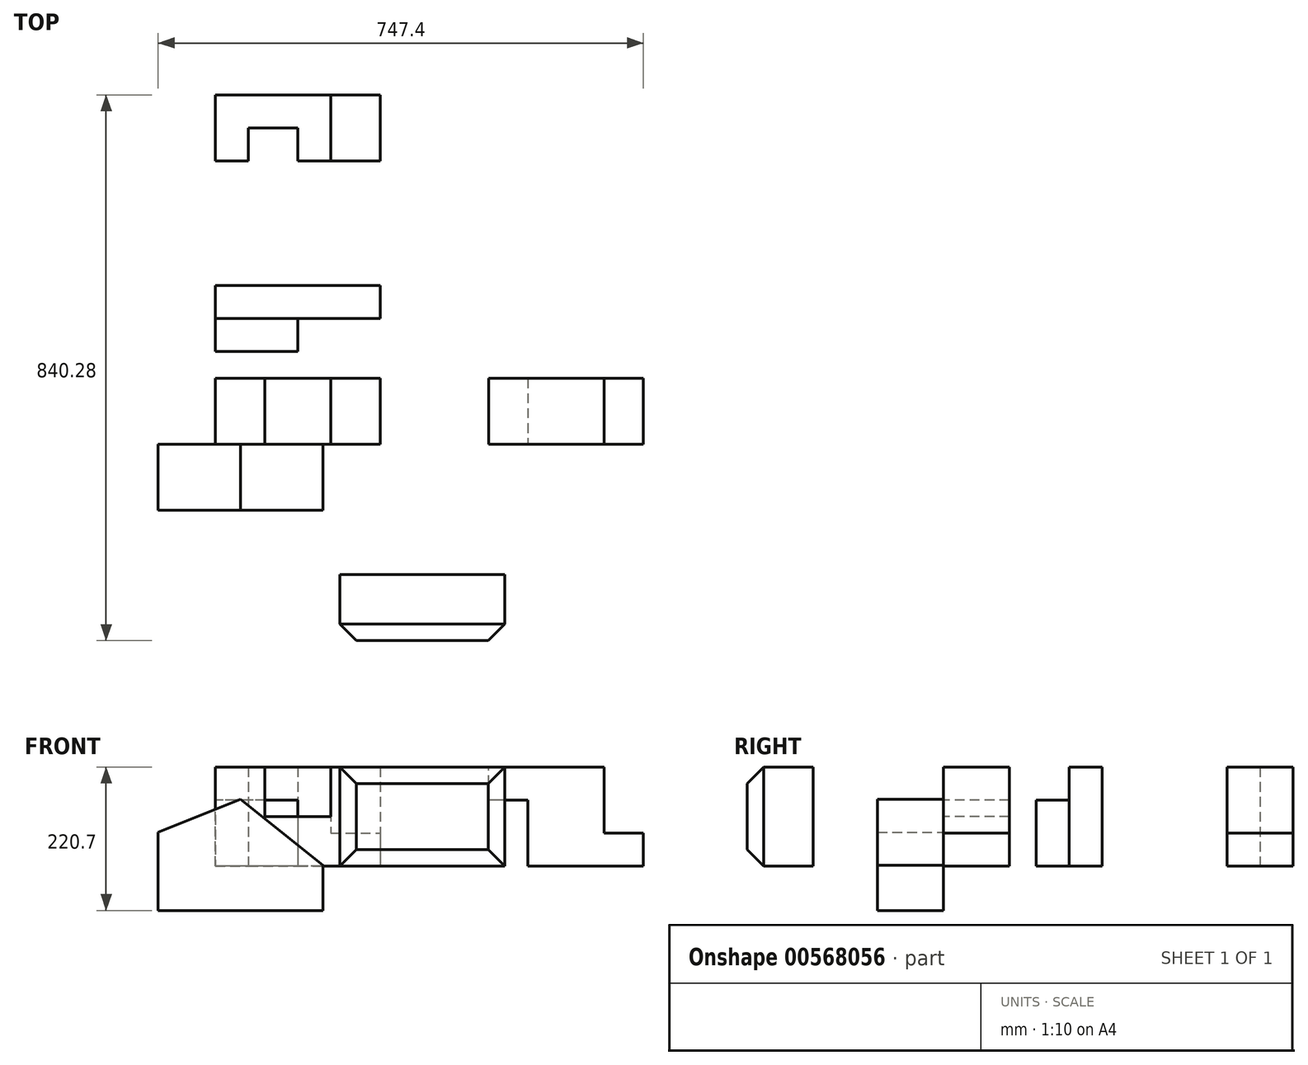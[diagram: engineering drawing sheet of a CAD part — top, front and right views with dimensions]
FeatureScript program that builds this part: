
annotation { "Feature Type Name" : "Feature", "Feature Type Description" : "" }
export const myFeature = defineFeature(function(context is Context, id is Id, definition is map)
    precondition{}
    {
        {
            var Q0;
            Q0=qCreatedBy(makeId("Front.planeOp"),FACE);
            var sketch = newSketch(context, id + "F0", { "sketchPlane" : qUnion([Q0])});
            skLineSegment(sketch, "E0", {"start": v(0, 0) * mm, "end": v(0, 152.4) * mm});
            skLineSegment(sketch, "E1", {"start": v(0, 152.4) * mm, "end": v(76.2, 152.4) * mm});
            skLineSegment(sketch, "E2", {"start": v(76.2, 152.4) * mm, "end": v(76.2, 76.2) * mm});
            skLineSegment(sketch, "E3", {"start": v(76.2, 76.2) * mm, "end": v(177.8, 76.2) * mm});
            skLineSegment(sketch, "E4", {"start": v(177.8, 76.2) * mm, "end": v(177.8, 152.4) * mm});
            skLineSegment(sketch, "E5", {"start": v(177.8, 152.4) * mm, "end": v(254, 152.4) * mm});
            skLineSegment(sketch, "E6", {"start": v(254, 152.4) * mm, "end": v(254, 0) * mm});
            skLineSegment(sketch, "E7", {"start": v(254, 0) * mm, "end": v(0, 0) * mm});
            skSolve(sketch);
        }
        {
            var Q0;
            Q0=makeQuery(id+"F0.imprint","IMPRINT",FACE,{"disambiguationData":[TD([[makeQuery(id+"F0.imprint","IMPRINT",EDGE,{"derivedFrom":sQuery(id+"F0.wireOp",EDGE,"E0")}),-1.0]])]});
            extrude(context, id + "F1", {"entities" : qUnion([Q0]), "oppositeDirection" : true, "depth" : 101.6 * mm, "offsetDistance" : 25.4 * mm});
        }
        {
            var Q0;
            Q0=qCreatedBy(makeId("Right.planeOp"),FACE);
            var sketch = newSketch(context, id + "F2", { "sketchPlane" : qUnion([Q0])});
            skLineSegment(sketch, "E8", {"start": v(170.6, 0) * mm, "end": v(244.48, 0) * mm});
            skLineSegment(sketch, "E9", {"start": v(244.48, 0) * mm, "end": v(244.48, 152.4) * mm});
            skLineSegment(sketch, "E10", {"start": v(244.48, 152.4) * mm, "end": v(193.68, 152.4) * mm});
            skLineSegment(sketch, "E11", {"start": v(193.68, 152.4) * mm, "end": v(193.68, 101.6) * mm});
            skLineSegment(sketch, "E12", {"start": v(193.68, 101.6) * mm, "end": v(142.88, 101.6) * mm});
            skLineSegment(sketch, "E13", {"start": v(142.88, 101.6) * mm, "end": v(142.88, 0) * mm});
            skLineSegment(sketch, "E14", {"start": v(142.88, 0) * mm, "end": v(170.6, 0) * mm});
            skSolve(sketch);
        }
        {
            var Q0;
            Q0=makeQuery(id+"F2.imprint","IMPRINT",FACE,{"disambiguationData":[TD([[makeQuery(id+"F2.imprint","IMPRINT",EDGE,{"derivedFrom":sQuery(id+"F2.wireOp",EDGE,"E8")}),1.0]])]});
            extrude(context, id + "F3", {"entities" : qUnion([Q0]), "depth" : 254 * mm, "offsetDistance" : 25.4 * mm});
        }
        {
            var Q0;
            Q0=makeQuery(id+"F3.opExtrude","CAP_FACE",FACE,{"disambiguationData":[OSD([sQuery(id+"F2.wireOp",EDGE,"E8"),sQuery(id+"F2.wireOp",EDGE,"E9"),sQuery(id+"F2.wireOp",EDGE,"E10"),sQuery(id+"F2.wireOp",EDGE,"E11"),sQuery(id+"F2.wireOp",EDGE,"E12"),sQuery(id+"F2.wireOp",EDGE,"E13"),sQuery(id+"F2.wireOp",EDGE,"E14")])],"isStart":false});
            var sketch = newSketch(context, id + "F4", { "sketchPlane" : qUnion([Q0])});
            skLineSegment(sketch, "E15", {"start": v(142.88, 101.6) * mm, "end": v(193.68, 101.6) * mm});
            skLineSegment(sketch, "E16", {"start": v(193.68, 101.6) * mm, "end": v(193.68, 0) * mm});
            skLineSegment(sketch, "E17", {"start": v(193.68, 0) * mm, "end": v(142.88, 0) * mm});
            skLineSegment(sketch, "E18", {"start": v(142.88, 0) * mm, "end": v(142.88, 101.6) * mm});
            skSolve(sketch);
        }
        {
            var Q0;
            Q0=makeQuery(id+"F4.imprint","IMPRINT",FACE,{"disambiguationData":[TD([[makeQuery(id+"F4.imprint","IMPRINT",EDGE,{"derivedFrom":sQuery(id+"F4.wireOp",EDGE,"E15")}),1.0]])]});
            extrude(context, id + "F5", {"entities" : qUnion([Q0]), "operationType" : NewBodyOperationType.REMOVE, "oppositeDirection" : true, "depth" : 127 * mm, "offsetDistance" : 25.4 * mm});
        }
        {
            var Q0;
            Q0=qCreatedBy(makeId("Top.planeOp"),FACE);
            var sketch = newSketch(context, id + "F6", { "sketchPlane" : qUnion([Q0])});
            skLineSegment(sketch, "E19", {"start": v(0, 436.67) * mm, "end": v(50.8, 436.67) * mm});
            skLineSegment(sketch, "E20", {"start": v(50.8, 436.67) * mm, "end": v(50.8, 487.47) * mm});
            skLineSegment(sketch, "E21", {"start": v(50.8, 487.47) * mm, "end": v(127, 487.47) * mm});
            skLineSegment(sketch, "E22", {"start": v(127, 487.47) * mm, "end": v(127, 436.67) * mm});
            skLineSegment(sketch, "E23", {"start": v(127, 436.67) * mm, "end": v(254, 436.67) * mm});
            skLineSegment(sketch, "E24", {"start": v(254, 436.67) * mm, "end": v(254, 538.27) * mm});
            skLineSegment(sketch, "E25", {"start": v(254, 538.27) * mm, "end": v(0, 538.27) * mm});
            skLineSegment(sketch, "E26", {"start": v(0, 538.27) * mm, "end": v(0, 436.67) * mm});
            skSolve(sketch);
        }
        {
            var Q0;
            Q0=makeQuery(id+"F6.imprint","IMPRINT",FACE,{"disambiguationData":[TD([[makeQuery(id+"F6.imprint","IMPRINT",EDGE,{"derivedFrom":sQuery(id+"F6.wireOp",EDGE,"E19")}),1.0]])]});
            extrude(context, id + "F7", {"entities" : qUnion([Q0]), "depth" : 152.4 * mm, "offsetDistance" : 25.4 * mm});
        }
        {
            var Q0;
            Q0=makeQuery(id+"F7.opExtrude","SWEPT_FACE",FACE,{"disambiguationData":[OSD([sQuery(id+"F6.wireOp",EDGE,"E23")])]});
            var sketch = newSketch(context, id + "F8", { "sketchPlane" : qUnion([Q0])});
            skSolve(sketch);
        }
        {
            var Q0;
            {var subQ0=sQuery(id+"F6.wireOp",EDGE,"E23");Q0=makeQuery(id+"F8.imprint","IMPRINT",FACE,{"disambiguationData":[TD([[makeQuery(id+"F8.imprint","IMPRINT",EDGE,{"derivedFrom":makeQuery(id+"F7.opExtrude","CAP_EDGE",EDGE,{"disambiguationData":[OSD([subQ0])],"isStart":true})}),1.0]])]});}
            var sketch = newSketch(context, id + "F9", { "sketchPlane" : qUnion([Q0])});
            skLineSegment(sketch, "E27.bottom", {"start": v(177.8, 152.4) * mm, "end": v(254, 152.4) * mm});
            skLineSegment(sketch, "E27.top", {"start": v(177.8, 50.8) * mm, "end": v(254, 50.8) * mm});
            skLineSegment(sketch, "E27.left", {"start": v(177.8, 152.4) * mm, "end": v(177.8, 50.8) * mm});
            skLineSegment(sketch, "E27.right", {"start": v(254, 152.4) * mm, "end": v(254, 50.8) * mm});
            skSolve(sketch);
        }
        {
            var Q0;
            Q0 = qSketchRegion(id + "F9", true);
            extrude(context, id + "F10", {"entities" : qUnion([Q0]), "operationType" : NewBodyOperationType.REMOVE, "oppositeDirection" : true, "depth" : 101.6 * mm, "offsetDistance" : 25.4 * mm});
        }
        {
            var Q0;
            Q0=qCreatedBy(makeId("Front.planeOp"),FACE);
            var sketch = newSketch(context, id + "F11", { "sketchPlane" : qUnion([Q0])});
            skLineSegment(sketch, "E28", {"start": v(481.39, 0) * mm, "end": v(481.39, 101.6) * mm});
            skLineSegment(sketch, "E29", {"start": v(481.39, 101.6) * mm, "end": v(420.78, 101.6) * mm});
            skLineSegment(sketch, "E30", {"start": v(420.78, 101.6) * mm, "end": v(420.78, 152.4) * mm});
            skLineSegment(sketch, "E31", {"start": v(420.78, 152.4) * mm, "end": v(598.58, 152.4) * mm});
            skLineSegment(sketch, "E32", {"start": v(598.58, 152.4) * mm, "end": v(598.58, 50.8) * mm});
            skLineSegment(sketch, "E33", {"start": v(598.58, 50.8) * mm, "end": v(659.19, 50.8) * mm});
            skLineSegment(sketch, "E34", {"start": v(659.19, 50.8) * mm, "end": v(659.19, 0) * mm});
            skLineSegment(sketch, "E35", {"start": v(659.19, 0) * mm, "end": v(481.39, 0) * mm});
            skSolve(sketch);
        }
        {
            var Q0;
            Q0=makeQuery(id+"F11.imprint","IMPRINT",FACE,{"disambiguationData":[TD([[makeQuery(id+"F11.imprint","IMPRINT",EDGE,{"derivedFrom":sQuery(id+"F11.wireOp",EDGE,"E28")}),-1.0]])]});
            extrude(context, id + "F12", {"entities" : qUnion([Q0]), "oppositeDirection" : true, "depth" : 101.6 * mm, "offsetDistance" : 25.4 * mm});
        }
        {
            var Q0;
            Q0=qCreatedBy(makeId("Front.planeOp"),FACE);
            var sketch = newSketch(context, id + "F13", { "sketchPlane" : qUnion([Q0])});
            skLineSegment(sketch, "E36", {"start": v(-88.21, -68.3) * mm, "end": v(-88.21, 52.23) * mm});
            skLineSegment(sketch, "E37", {"start": v(-88.21, 52.23) * mm, "end": v(38.79, 103.03) * mm});
            skLineSegment(sketch, "E38", {"start": v(38.79, 103.03) * mm, "end": v(165.79, 1.43) * mm});
            skLineSegment(sketch, "E39", {"start": v(165.79, 1.43) * mm, "end": v(165.79, -68.3) * mm});
            skLineSegment(sketch, "E40", {"start": v(165.79, -68.3) * mm, "end": v(-88.21, -68.3) * mm});
            skSolve(sketch);
        }
        {
            var Q0;
            Q0=makeQuery(id+"F13.imprint","IMPRINT",FACE,{"disambiguationData":[TD([[makeQuery(id+"F13.imprint","IMPRINT",EDGE,{"derivedFrom":sQuery(id+"F13.wireOp",EDGE,"E36")}),-1.0]])]});
            extrude(context, id + "F14", {"entities" : qUnion([Q0]), "operationType" : NewBodyOperationType.ADD, "depth" : 101.6 * mm, "offsetDistance" : 25.4 * mm});
        }
        {
            var Q0;
            Q0=qCreatedBy(makeId("Top.planeOp"),FACE);
            var sketch = newSketch(context, id + "F15", { "sketchPlane" : qUnion([Q0])});
            skLineSegment(sketch, "E41", {"start": v(191.91, -200.4) * mm, "end": v(445.91, -200.4) * mm});
            skLineSegment(sketch, "E42", {"start": v(445.91, -200.4) * mm, "end": v(445.91, -302) * mm});
            skLineSegment(sketch, "E43", {"start": v(445.91, -302) * mm, "end": v(191.91, -302) * mm});
            skLineSegment(sketch, "E44", {"start": v(191.91, -302) * mm, "end": v(191.91, -200.4) * mm});
            skSolve(sketch);
        }
        {
            var Q0;
            Q0=makeQuery(id+"F15.imprint","IMPRINT",FACE,{"disambiguationData":[TD([[makeQuery(id+"F15.imprint","IMPRINT",EDGE,{"derivedFrom":sQuery(id+"F15.wireOp",EDGE,"E41")}),-1.0]])]});
            extrude(context, id + "F16", {"entities" : qUnion([Q0]), "depth" : 152.4 * mm, "offsetDistance" : 25.4 * mm});
        }
        {
            var Q0;
            Q0=makeQuery(id+"F16.opExtrude","SWEPT_FACE",FACE,{"disambiguationData":[OSD([sQuery(id+"F15.wireOp",EDGE,"E43")])]});
            chamfer(context, id + "F17", {"entities" : qUnion([Q0]), "width" : 25.4 * mm, "tangentPropagation" : true});
        }
    });
